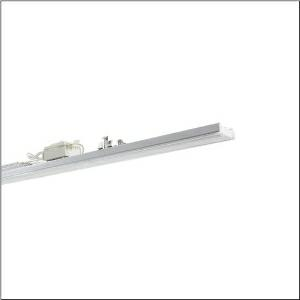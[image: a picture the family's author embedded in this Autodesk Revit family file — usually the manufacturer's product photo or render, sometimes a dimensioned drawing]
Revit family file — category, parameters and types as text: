
# Revit family: licross_11_recessed_mo_51te12dn4axg3s4
name_source: partatom
category: Lighting Fixtures
units: mm (PartAtom-declared; Revit-internal decimal feet)

## family parameters
Cut with Voids When Loaded = No
Host = Face
Light Source = No
Part Type = Normal
Room Calculation Point = No
Round Connector Dimension = Use Diameter
Shared = No

## types (1)
- --- (1 x LED, 1010 lm, 6.7 W, 4000K)
    Apparent Load = 7 VA
    CIE Flux Codes = 67 92 99 100 100
    Color Rendering = 80
    Color Temperature = 4000K
    Default Elevation = 1800 mm
    Description = Licross 11 Recessed MO, luminaire insert, of sheet steel, galvanised, coil coated, white, length: 1.500mm, width: 66mm, height: 67mm, LED rated luminous flux: 10.240lm, light colour: 840, SDCM (Standard Deviation of Colour Matching)MacAdam ≤ 2 SDCM (initial), control gear: DALI 2, with plug, 6-pole, with phase selection, for trunking rail, 9 or 11-core, mains connection: 220..240V, AC, 50/60Hz, rated input power: 61W, for trunking rail, 9-/11-core, internal wiring halogen-free, for emergency light function, converter,control gear: single battery element, battery: LiFePO4, 9Ah, primary optical cover: cover, of PMMA, light emission: direct distribution, primary light characteristic: symmetric, protection rating (complete): IP54, insulation class (complete): insulation class I (protective earthing), certification: CE, UKCA, protection symbol: D if used in an environment with non-conductive dust loads with corresponding accessories, impact resistance: IK06, permissible ambient temperature for indoor applications: +5..+35°C, standard: EN 60598-2-22, LABS conformity tested according to VDMA 24364:2018-05, reducing of maximum allowable ambient temperature of 5°C with ceiling mounting, corresponds to IFS (International Featured Standards) requirements for safety and quality in the food industry, The light source and the operating device comply with the requirements of the Ecodesign Regulation (EU) 2019/2020 and are replaceable in accordance with this regulation, packaging unit: 1 piece
    Height = 58 mm
    Lamp = 1 x LED
    Lamp Light Flux = 1010 lm
    Lamp Power = 6.7 W
    Lamp count = 1
    Length = 1500 mm
    Luminous efficacy = 151 lm/W
    Manufacturer = Siteco
    ModVariant = No
    Model = 51TE12DN4AXG3S4
    Mounting Place = Ceiling
    Mounting Type = Pendant
    Number of Poles = 1
    OnlyDefault = Yes
    Power Factor = 1
    Product Name = Licross 11 Recessed MO
    Product group = luminaire insert | ceiling pendant
    ProductGroupID = 901
    Protection Class = Protection class I
    Protection Degree = IP 54
    RLX_Detail_Level = 1
    RLX_Emergency_Light_Flux = 0 lm
    RLX_Emergency_Type = 0
    RLX_Emergency_Type_DB = No
    RlxData = <blob elided: 25057 chars, md5=385406bb>
    Socket = socket
    Standby Power = 0 W
    System Light Flux = 1010 lm
    System Power = 7 W
    Type Comments = : emergency light operation: 3 h
    Type Image = l_1296930.jpg
    URL = http://relux.com
    VarID = @adj_094015
    Voltage = 0 V
    Weight = 0.00 kg
    Width = 66 mm

## geometry (parser evidence)
native form markers: Blend x4, Sweep x12
no freeform markers — native parametric forms only
